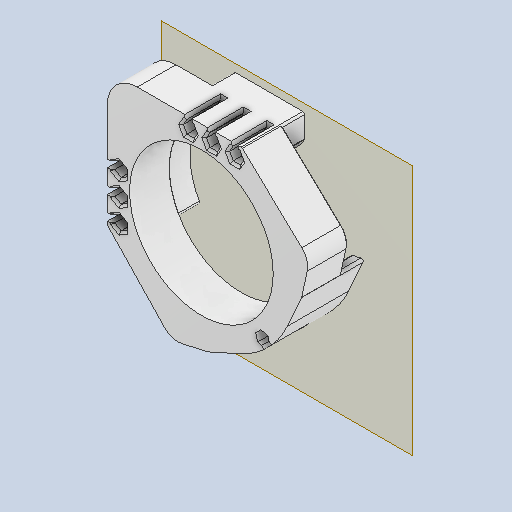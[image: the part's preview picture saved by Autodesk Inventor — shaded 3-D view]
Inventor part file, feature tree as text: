
AUTODESK INVENTOR PART (.ipt)
format: ipt  version: 2022 (Build 260153000, 153)  size: 543,744 bytes
history: native  units: in
note: dims shown in document units (in); Inventor stores cm internally (conversion verified against a paired STEP export)
features: sketch x5, other x3, plane x2
ambient origin geometry x8: Origin, YZ Plane, XZ Plane, XY Plane, X Axis, Y Axis, Z Axis, Center Point
bodies: Solid1 (feature_tree)
feature tree (10):
  other  "upper_MIR.ipt"
  other  "Solid1::upper_MIR.ipt"
  other  "TaggingFeature1"
  sketch  "Sketch1"  dims[d0=0.3937in]
  sketch  "Sketch2"
  sketch  "Sketch3"
  sketch  "Sketch5"
  sketch  "Sketch6"
  plane  "Work Plane1"
  plane  "Work Plane2"
